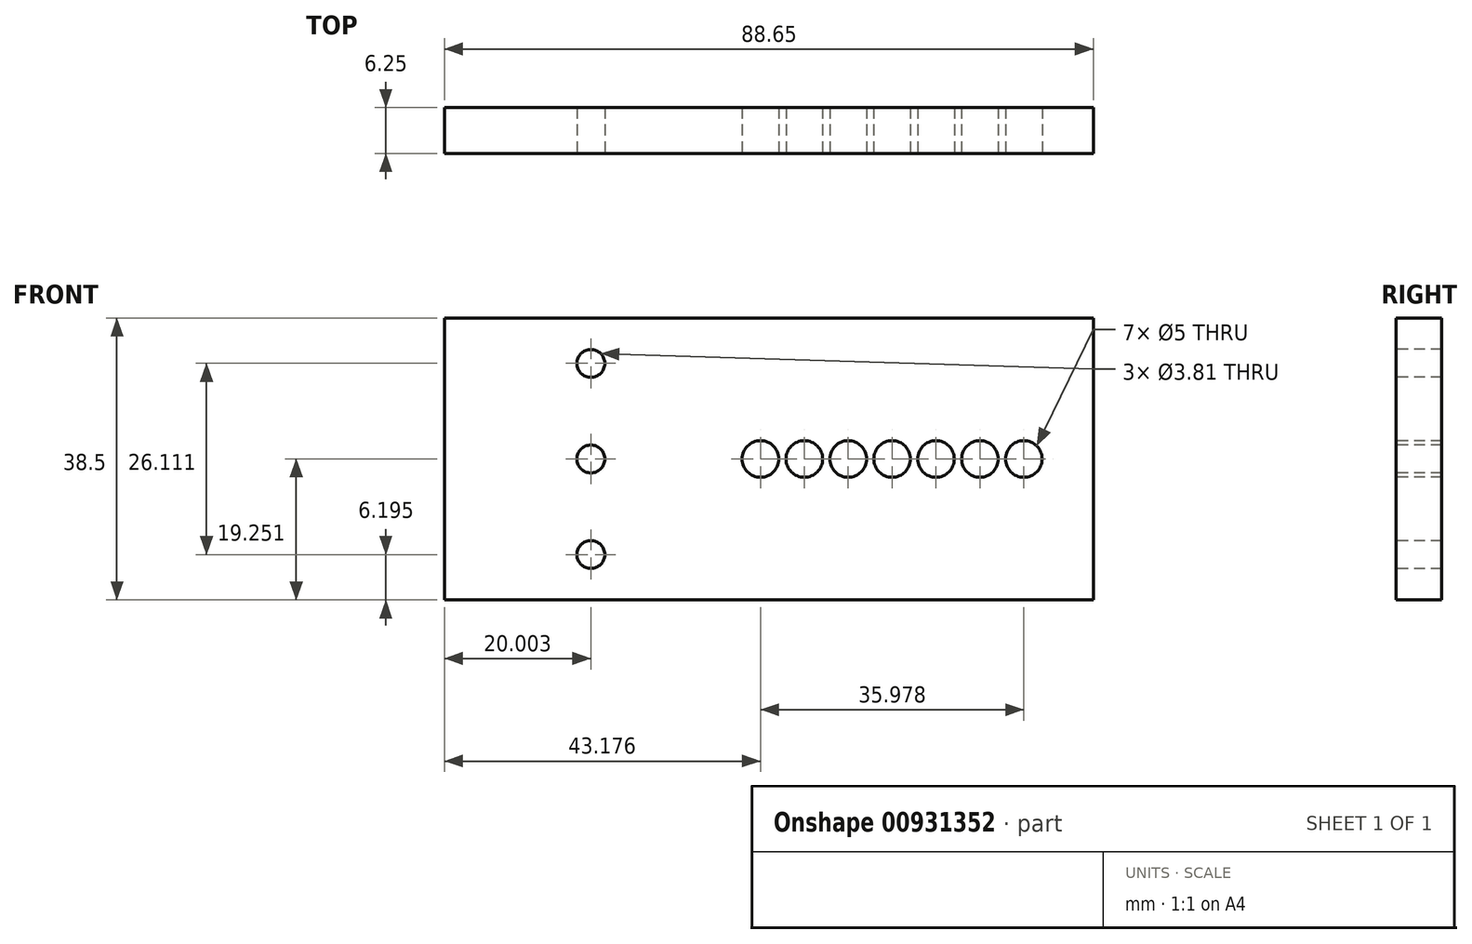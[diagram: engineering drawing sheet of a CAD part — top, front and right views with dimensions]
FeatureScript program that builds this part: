
annotation { "Feature Type Name" : "Feature", "Feature Type Description" : "" }
export const myFeature = defineFeature(function(context is Context, id is Id, definition is map)
    precondition{}
    {
        {
            var Q0;
            Q0=qCreatedBy(makeId("Front.planeOp"),FACE);
            var sketch = newSketch(context, id + "F0", { "sketchPlane" : qUnion([Q0])});
            skLineSegment(sketch, "E0.bottom", {"start": v(-39.78, 16.51) * mm, "end": v(48.87, 16.51) * mm});
            skLineSegment(sketch, "E0.top", {"start": v(-39.78, -22) * mm, "end": v(48.87, -22) * mm});
            skLineSegment(sketch, "E0.left", {"start": v(-39.78, 16.51) * mm, "end": v(-39.78, -22) * mm});
            skLineSegment(sketch, "E0.right", {"start": v(48.87, 16.51) * mm, "end": v(48.87, -22) * mm});
            skCircle(sketch, "E1", {"center": v(-19.78, 10.32) * mm, "radius": 1.9 * mm});
            skCircle(sketch, "E2", {"center": v(-19.78, -2.74) * mm, "radius": 1.9 * mm});
            skCircle(sketch, "E3", {"center": v(-19.78, -15.8) * mm, "radius": 1.9 * mm});
            skLineSegment(sketch, "E4", {"start": v(-39.78, -2.74) * mm, "end": v(48.87, -2.74) * mm, "construction": true});
            skCircle(sketch, "E5", {"center": v(9.39, -2.74) * mm, "radius": 2.5 * mm});
            skCircle(sketch, "E6", {"center": v(15.38, -2.74) * mm, "radius": 2.5 * mm});
            skCircle(sketch, "E7", {"center": v(21.38, -2.74) * mm, "radius": 2.5 * mm});
            skCircle(sketch, "E8", {"center": v(27.37, -2.74) * mm, "radius": 2.5 * mm});
            skCircle(sketch, "E9", {"center": v(33.37, -2.74) * mm, "radius": 2.5 * mm});
            skCircle(sketch, "E10", {"center": v(39.37, -2.74) * mm, "radius": 2.5 * mm});
            skCircle(sketch, "E11", {"center": v(3.4, -2.74) * mm, "radius": 2.5 * mm});
            skSolve(sketch);
        }
        {
            var Q0;
            Q0=makeQuery(id+"F0.imprint","IMPRINT",FACE,{"disambiguationData":[TD([[makeQuery(id+"F0.imprint","IMPRINT",EDGE,{"derivedFrom":sQuery(id+"F0.wireOp",EDGE,"E0.bottom")}),-1.0]])]});
            extrude(context, id + "F1", {"entities" : qUnion([Q0]), "oppositeDirection" : true, "depth" : 6.25 * mm, "offsetDistance" : 25.4 * mm});
        }
    });
